# Revit family: QF_COMENDA_6G3211_PA_AA
name_source: partatom
category: Attrezzature speciali
units: mm (PartAtom-declared; Revit-internal decimal feet)

## family parameters
Basato su piano di lavoro = No
Condiviso = No
Numero OmniClass = 23.40.40.14
Punto di calcolo locali = No
Quota connettore circolare = Usa diametro
Sempre verticale = Sì
Taglio con vuoti quando caricato = No
Tipo di parte = Normale
Titolo OmniClass = Food Service Equipment

## types (1)
- 6G3211_PA_AA
    Altezza = 2145 mm  [stored 7.0374 ft]
    Altezza allacciamento elettrico da pavimento finito = 365 mm  [stored 1.19751 ft]
    Altezza da terra raccordo acqua calda = 230 mm  [stored 0.754593 ft]
    Altezza dello scarico diretto acqua da pavimento finito = 230 mm  [stored 0.754593 ft]
    Corrente di funzionamento normale = 12 A
    Descrizione = THREE-PHASE FRONT LOADING POTWASHER WITH CRC
    Diametro dello scarico diretto di acqua = 1 1/2"
    Diametro raccordo acqua calda = 1"
    Fase = 3
    Frequenza = 50 Hz
    Lunghezza = 740 mm  [stored 2.42782 ft]
    Modello = Gi 505 CRC
    Numero dei poli = 3
    Peso netto = 150.00 kg
    Potenza elettrica = 7500 W
    Pressione minima acqua calda = 2000.0 Pa
    Produttore = COMENDA
    Profondità = 845 mm  [stored 2.77231 ft]
    Prospetto di default = 0 mm  [stored 0 ft]
    Protezione contro le sovracorrenti = 16 A
    Temperatura raccomandata per acqua calda = 50 °C
    Tensione = 380 V
    URL = www.comenda.fr
    URL catalogo = https://www.comenda.fr

note: [stored X ft] marks values corroborated as IEEE doubles in the binary element streams (Revit-internal decimal feet)

## geometry (parser evidence)
native form markers: Sweep x4
no freeform markers — native parametric forms only
